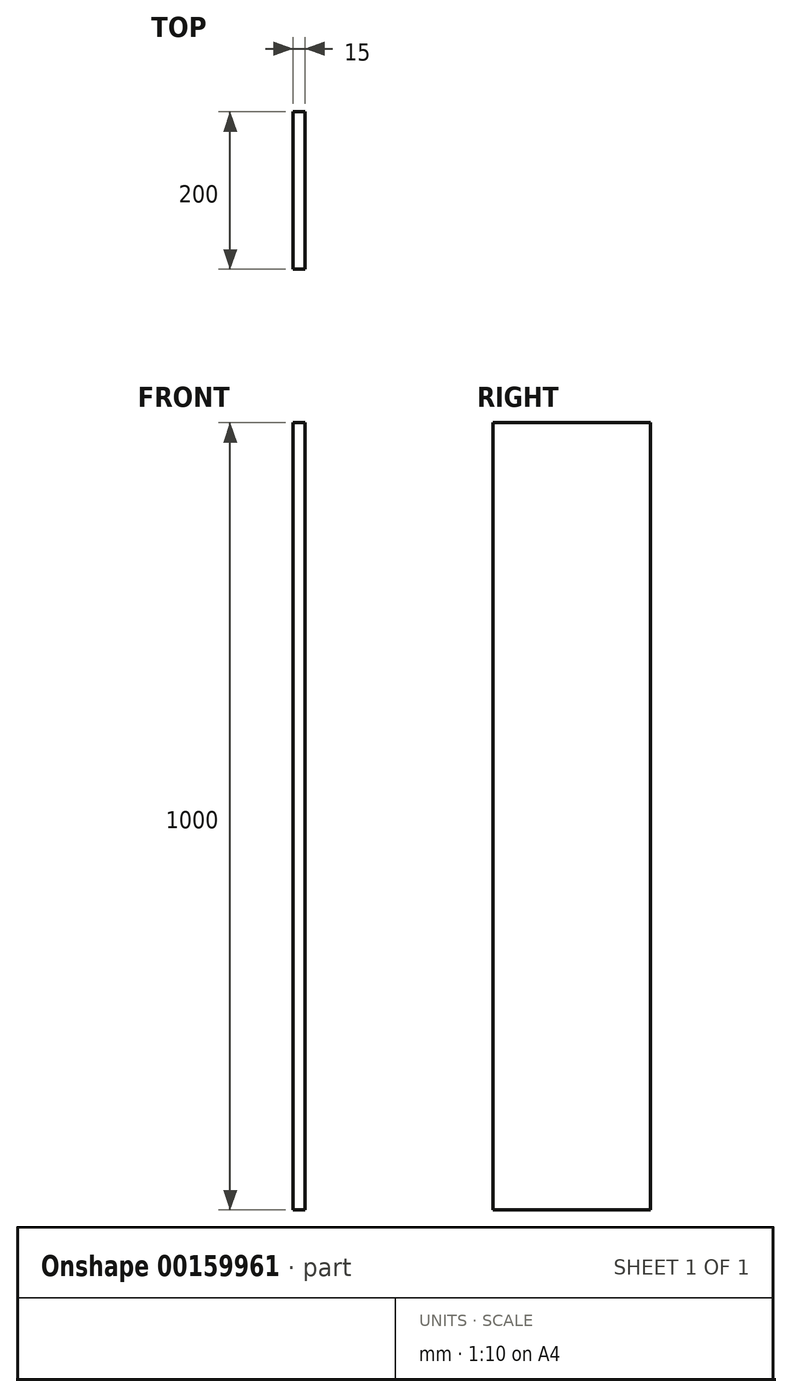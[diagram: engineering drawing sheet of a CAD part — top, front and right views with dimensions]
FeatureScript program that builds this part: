
annotation { "Feature Type Name" : "Feature", "Feature Type Description" : "" }
export const myFeature = defineFeature(function(context is Context, id is Id, definition is map)
    precondition{}
    {
        {
            var Q0;
            Q0=qCreatedBy(makeId("Right.planeOp"),FACE);
            var sketch = newSketch(context, id + "F0", { "sketchPlane" : qUnion([Q0])});
            skLineSegment(sketch, "E0.bottom", {"start": v(-117.97, 865.49) * mm, "end": v(82.03, 865.49) * mm});
            skLineSegment(sketch, "E0.top", {"start": v(-117.97, -134.51) * mm, "end": v(82.03, -134.51) * mm});
            skLineSegment(sketch, "E0.left", {"start": v(-117.97, 865.49) * mm, "end": v(-117.97, -134.51) * mm});
            skLineSegment(sketch, "E0.right", {"start": v(82.03, 865.49) * mm, "end": v(82.03, -134.51) * mm});
            skSolve(sketch);
        }
        {
            var Q0;
            Q0=makeQuery(id+"F0.imprint","IMPRINT",FACE,{"disambiguationData":[TD([[makeQuery(id+"F0.imprint","IMPRINT",EDGE,{"derivedFrom":sQuery(id+"F0.wireOp",EDGE,"E0.bottom")}),-1.0]])]});
            extrude(context, id + "F1", {"entities" : qUnion([Q0]), "depth" : 15 * mm});
        }
    });
